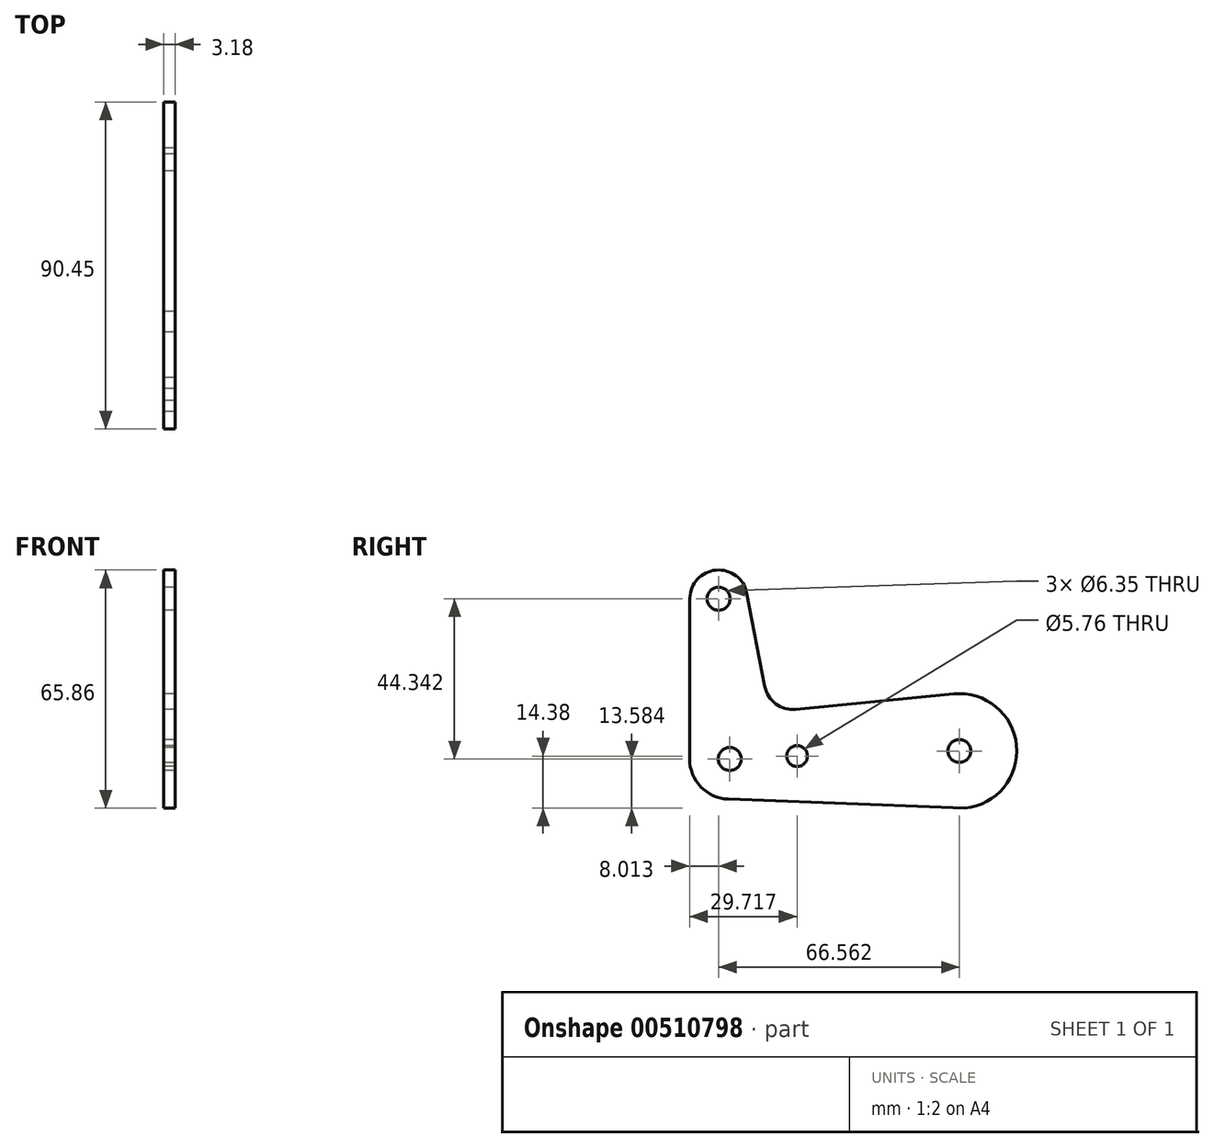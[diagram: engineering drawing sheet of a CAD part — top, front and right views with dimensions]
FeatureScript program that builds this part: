
annotation { "Feature Type Name" : "Feature", "Feature Type Description" : "" }
export const myFeature = defineFeature(function(context is Context, id is Id, definition is map)
    precondition{}
    {
        {
            var Q0;
            Q0=qCreatedBy(makeId("Right.planeOp"),FACE);
            var sketch = newSketch(context, id + "F0", { "sketchPlane" : qUnion([Q0])});
            skLineSegment(sketch, "E0", {"start": v(-26.18, -12.3) * mm, "end": v(-23.93, -14.55) * mm, "construction": true});
            skLineSegment(sketch, "E1", {"start": v(5.25, -43.74) * mm, "end": v(7.58, -41.58) * mm, "construction": true});
            skCircle(sketch, "E2", {"center": v(-26.18, -12.3) * mm, "radius": 3.18 * mm});
            skCircle(sketch, "E3", {"center": v(5.25, -43.74) * mm, "radius": 3.18 * mm});
            skCircle(sketch, "E4", {"center": v(51.7, -0.44) * mm, "radius": 3.18 * mm});
            skArc(sketch, "E5", {"start": v(-21.28, -6.06) * mm, "mid": v(-31.95, -6.86) * mm, "end": v(-32.13, -17.56) * mm});
            skArc(sketch, "E6", {"start": v(-3.14, -51.02) * mm, "mid": v(4.26, -54.8) * mm, "end": v(12.22, -52.4) * mm});
            skArc(sketch, "E7", {"start": v(59.87, -14.05) * mm, "mid": v(64.08, 9.5) * mm, "end": v(40.17, 10.47) * mm});
            skLineSegment(sketch, "E8", {"start": v(-32.22, -17.45) * mm, "end": v(-3.14, -51.02) * mm});
            skLineSegment(sketch, "E9", {"start": v(-0.68, -22.2) * mm, "end": v(-21.28, -6.06) * mm});
            skArc(sketch, "E10.filletArc", {"start": v(-0.68, -22.2) * mm, "mid": v(4.84, -23.88) * mm, "end": v(10.04, -21.37) * mm});
            skLineSegment(sketch, "E11", {"start": v(10.04, -21.37) * mm, "end": v(40.19, 10.5) * mm});
            skLineSegment(sketch, "E12", {"start": v(63.25, -11.33) * mm, "end": v(12.22, -52.4) * mm});
            skLineSegment(sketch, "E13.trimOffspring", {"start": v(3, -41.5) * mm, "end": v(5.25, -43.74) * mm, "construction": true});
            skCircle(sketch, "E14", {"center": v(18.77, -30.94) * mm, "radius": 2.88 * mm});
            skSolve(sketch);
        }
        {
            var Q0;
            Q0=makeQuery(id+"F0.imprint","IMPRINT",FACE,{"disambiguationData":[TD([[makeQuery(id+"F0.imprint","IMPRINT",EDGE,{"derivedFrom":sQuery(id+"F0.wireOp",EDGE,"E2")}),-1.0]])]});
            extrude(context, id + "F1", {"entities" : qUnion([Q0]), "depth" : 3.17 * mm, "offsetDistance" : 25.4 * mm});
        }
        {
            var Q0;
            Q0=qCreatedBy(makeId("Front.planeOp"),FACE);
            var sketch = newSketch(context, id + "F2", { "sketchPlane" : qUnion([Q0])});
            skLineSegment(sketch, "E15", {"start": v(42.3, 21.45) * mm, "end": v(-53.6, 21.45) * mm});
            skSolve(sketch);
        }
        {
            var Q0;
            Q0=makeQuery(id+"F1.opExtrude","SWEPT_BODY",BODY,{"disambiguationData":[OSD([sQuery(id+"F0.wireOp",EDGE,"E2"),sQuery(id+"F0.wireOp",EDGE,"E3"),sQuery(id+"F0.wireOp",EDGE,"E4"),sQuery(id+"F0.wireOp",EDGE,"E5"),sQuery(id+"F0.wireOp",EDGE,"E6"),sQuery(id+"F0.wireOp",EDGE,"E7"),sQuery(id+"F0.wireOp",EDGE,"E8"),sQuery(id+"F0.wireOp",EDGE,"E9"),sQuery(id+"F0.wireOp",EDGE,"E10.filletArc"),sQuery(id+"F0.wireOp",EDGE,"E11"),sQuery(id+"F0.wireOp",EDGE,"E12"),sQuery(id+"F0.wireOp",EDGE,"E14")])]});
            var Q1;
            Q1=sQuery(id+"F2.wireOp",EDGE,"E15");
            var Q2;
            Q2=sQuery(id+"F2.wireOp",EDGE,"E15");
            transform(context, id + "F3", {"entities" : qUnion([Q0]), "transformType" : TransformType.ROTATION, "transformAxis" : qUnion([Q2]), "angle" : 41 * degree, "makeCopy" : false});
        }
    });
